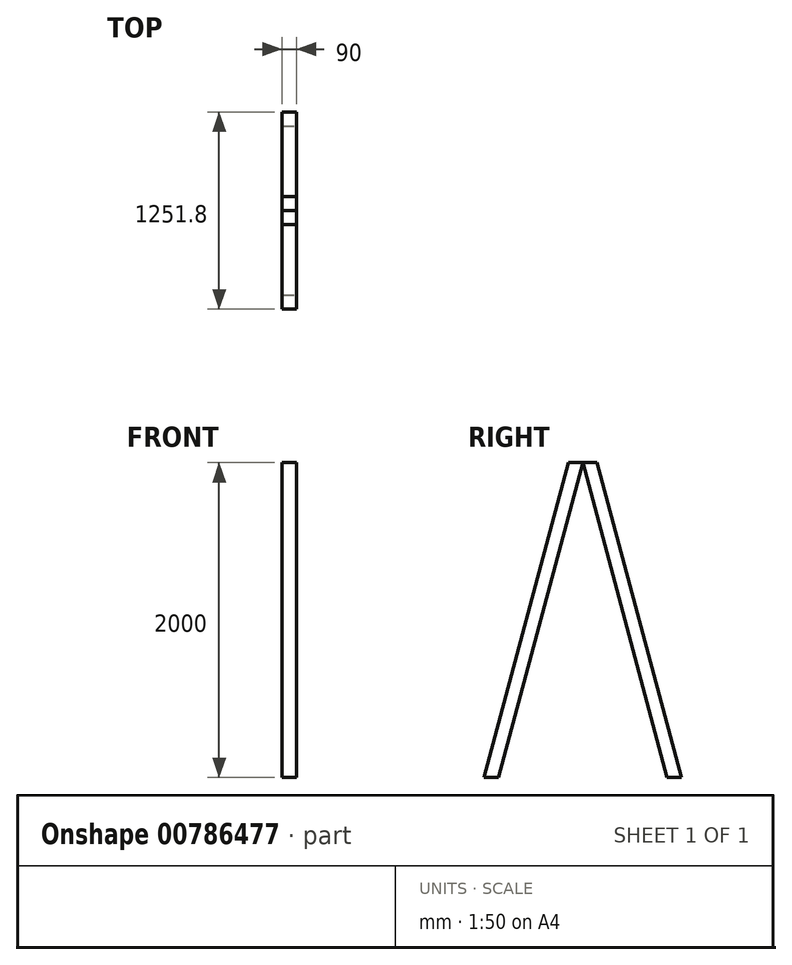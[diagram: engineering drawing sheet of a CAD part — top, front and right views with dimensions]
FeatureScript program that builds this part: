
annotation { "Feature Type Name" : "Feature", "Feature Type Description" : "" }
export const myFeature = defineFeature(function(context is Context, id is Id, definition is map)
    precondition{}
    {
        {
            var Q0;
            Q0=qCreatedBy(makeId("Right.planeOp"),FACE);
            var sketch = newSketch(context, id + "F0", { "sketchPlane" : qUnion([Q0])});
            skLineSegment(sketch, "E0", {"start": v(0, 0) * mm, "end": v(769.63, 0) * mm});
            skLineSegment(sketch, "E1.0", {"start": v(0, 2000) * mm, "end": v(966.55, 2000) * mm});
            skLineSegment(sketch, "E2", {"start": v(483.27, 2000) * mm, "end": v(483.27, 0) * mm});
            skLineSegment(sketch, "E3", {"start": v(483.27, 2000) * mm, "end": v(-52.63, 0) * mm});
            skLineSegment(sketch, "E4", {"start": v(483.27, 2000) * mm, "end": v(1019.17, 0) * mm});
            skSolve(sketch);
        }
        {
            var Q0;
            Q0=qCreatedBy(makeId("Top.planeOp"),FACE);
            var sketch = newSketch(context, id + "F1", { "sketchPlane" : qUnion([Q0])});
            skPoint(sketch, "E5.0", {"position": v(0, 1019.17) * mm});
            skLineSegment(sketch, "E6.bottom", {"start": v(0, 1019.17) * mm, "end": v(90, 1019.17) * mm});
            skLineSegment(sketch, "E6.top", {"start": v(0, 1109.17) * mm, "end": v(90, 1109.17) * mm});
            skLineSegment(sketch, "E6.left", {"start": v(0, 1019.17) * mm, "end": v(0, 1109.17) * mm});
            skLineSegment(sketch, "E6.right", {"start": v(90, 1019.17) * mm, "end": v(90, 1109.17) * mm});
            skPoint(sketch, "E7.0", {"position": v(0, -52.63) * mm});
            skLineSegment(sketch, "E8.bottom", {"start": v(0, -52.63) * mm, "end": v(90, -52.63) * mm});
            skLineSegment(sketch, "E8.top", {"start": v(0, -142.63) * mm, "end": v(90, -142.63) * mm});
            skLineSegment(sketch, "E8.left", {"start": v(0, -52.63) * mm, "end": v(0, -142.63) * mm});
            skLineSegment(sketch, "E8.right", {"start": v(90, -52.63) * mm, "end": v(90, -142.63) * mm});
            skSolve(sketch);
        }
        {
            var Q0;
            Q0=makeQuery(id+"F1.imprint","IMPRINT",FACE,{"disambiguationData":[TD([[makeQuery(id+"F1.imprint","IMPRINT",EDGE,{"derivedFrom":sQuery(id+"F1.wireOp",EDGE,"E6.bottom")}),1.0]])]});
            var Q1;
            Q1=sQuery(id+"F0.wireOp",EDGE,"E4");
            sweep(context, id + "F2", {"profiles" : qUnion([Q0]), "path" : qUnion([Q1])});
        }
        {
            var Q0;
            Q0=makeQuery(id+"F1.imprint","IMPRINT",FACE,{"disambiguationData":[TD([[makeQuery(id+"F1.imprint","IMPRINT",EDGE,{"derivedFrom":sQuery(id+"F1.wireOp",EDGE,"E8.bottom")}),-1.0]])]});
            var Q1;
            Q1=sQuery(id+"F0.wireOp",EDGE,"E3");
            sweep(context, id + "F3", {"profiles" : qUnion([Q0]), "path" : qUnion([Q1])});
        }
    });
